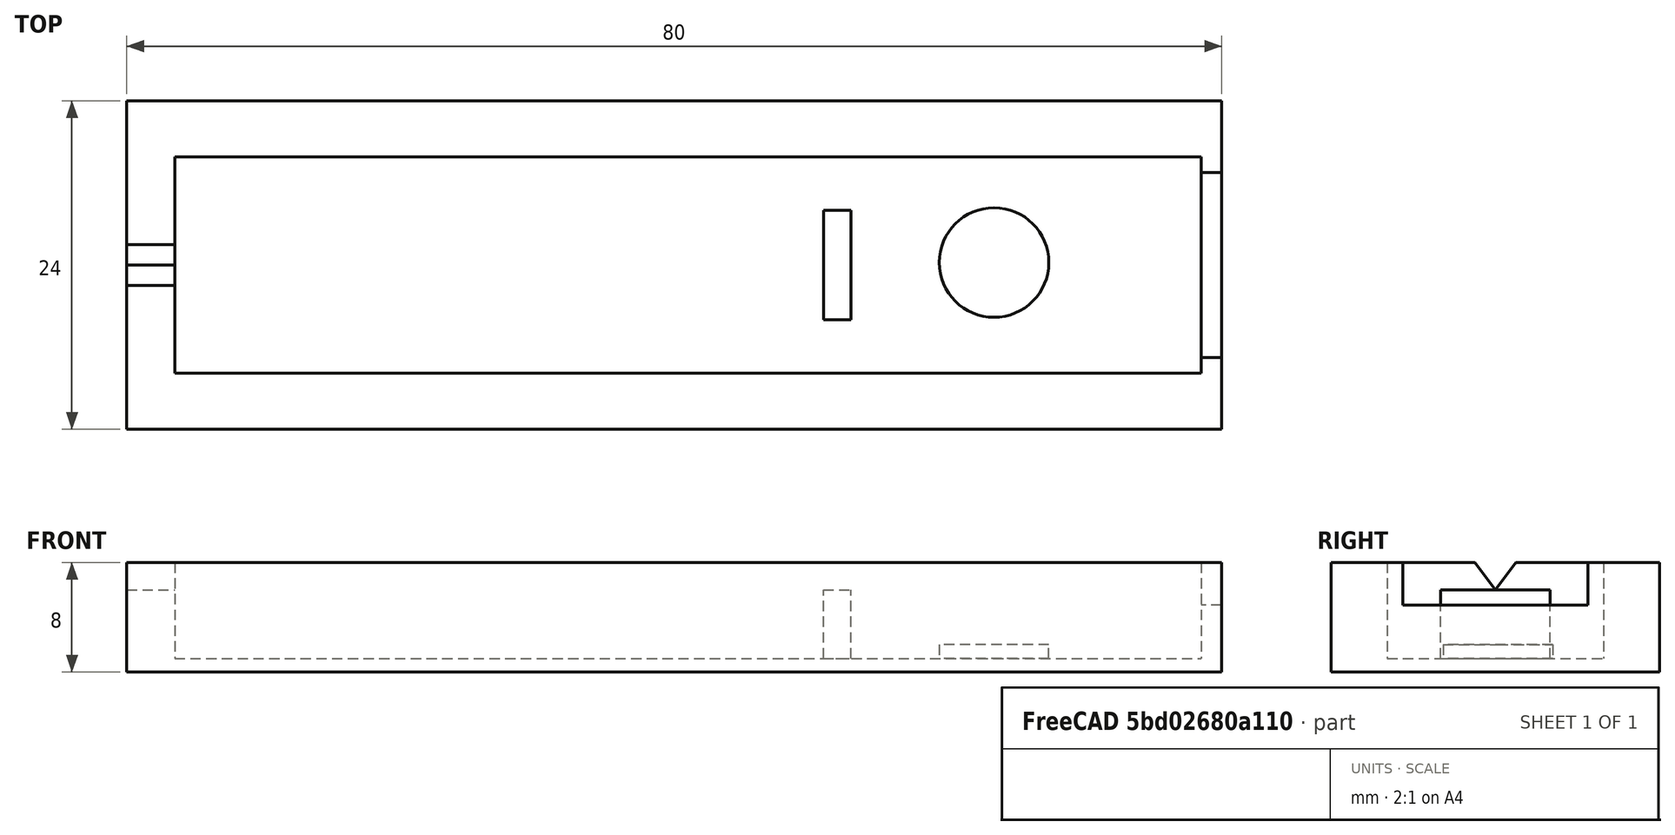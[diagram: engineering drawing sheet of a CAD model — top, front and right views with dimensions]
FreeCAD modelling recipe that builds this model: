
FCSTD DOCUMENT  (FreeCAD 0.19R)
Label: ChargerBuckOnly1
License: All rights reserved
LicenseURL: http://en.wikipedia.org/wiki/All_rights_reserved
objects: Sketcher::SketchObject×7, PartDesign::Pad×3, PartDesign::Pocket×3, PartDesign::Body×1, Mesh::Feature×1
note: 20 computed .brp shape members not serialized (recipe doc carries the construction recipe); baked Part::Feature solids carry a one-line shape summary decoded from their .brp

FEATURE [Sketcher::SketchObject] Sketch
  FullyConstrained = true
  MapMode = 5
  Support = -> [XY_Plane]
  sketch-geometry (4):
    g0: LineSegment StartX=-40 StartY=12 StartZ=0 EndX=40 EndY=12 EndZ=0
    g1: LineSegment StartX=40 StartY=12 StartZ=0 EndX=40 EndY=-12 EndZ=0
    g2: LineSegment StartX=40 StartY=-12 StartZ=0 EndX=-40 EndY=-12 EndZ=0
    g3: LineSegment StartX=-40 StartY=-12 StartZ=0 EndX=-40 EndY=12 EndZ=0
  constraints (11):
    c: Coincident(g0,g1)
    c: Coincident(g1,g2)
    c: Coincident(g2,g3)
    c: Coincident(g3,g0)
    c: Horizontal(g0)
    c: Horizontal(g2)
    c: Vertical(g1)
    c: Vertical(g3)
    c: Symmetric(g0,g2,g-1)
    c: Distance(g1) = 24
    c: Distance(g0,g0) = 80
FEATURE [PartDesign::Pad] Pad
  Direction = (1,1,1)
  Length = 8
  Length2 = 100
  Profile = -> Sketch
  Type = 0
FEATURE [Sketcher::SketchObject] Sketch001
  ExternalGeometry = -> [Pad]
  FullyConstrained = true
  MapMode = 5
  Placement = pos=(0,0,8) rot=(0,0,1;0rad)
  Support = -> [Pad]
  sketch-geometry (4):
    g0: LineSegment StartX=-36.5 StartY=7.9 StartZ=0 EndX=38.5 EndY=7.9 EndZ=0
    g1: LineSegment StartX=38.5 StartY=7.9 StartZ=0 EndX=38.5 EndY=-7.9 EndZ=0
    g2: LineSegment StartX=38.5 StartY=-7.9 StartZ=0 EndX=-36.5 EndY=-7.9 EndZ=0
    g3: LineSegment StartX=-36.5 StartY=-7.9 StartZ=0 EndX=-36.5 EndY=7.9 EndZ=0
  constraints (11):
    c: Coincident(g0,g1)
    c: Coincident(g1,g2)
    c: Coincident(g2,g3)
    c: Coincident(g3,g0)
    c: Horizontal(g0)
    c: Horizontal(g2)
    c: Vertical(g1)
    c: Distance(g0) = 75
    c: Distance(g1) = 15.8
    c: Distance(g1,g-3) = 1.5
    c: Symmetric(g0,g2,g-1)
FEATURE [PartDesign::Pocket] Pocket
  BaseFeature = -> Pad
  Length = 7
  Length2 = 100
  Profile = -> Sketch001
  Type = 0
FEATURE [Sketcher::SketchObject] Sketch002
  ExternalGeometry = -> [Pocket]
  FullyConstrained = true
  MapMode = 5
  Placement = pos=(0,0,1) rot=(0,0,1;0rad)
  Support = -> [Pocket]
  sketch-geometry (4):
    g0: LineSegment StartX=10.9 StartY=4 StartZ=0 EndX=12.9 EndY=4 EndZ=0
    g1: LineSegment StartX=12.9 StartY=4 StartZ=0 EndX=12.9 EndY=-4 EndZ=0
    g2: LineSegment StartX=12.9 StartY=-4 StartZ=0 EndX=10.9 EndY=-4 EndZ=0
    g3: LineSegment StartX=10.9 StartY=-4 StartZ=0 EndX=10.9 EndY=4 EndZ=0
  constraints (11):
    c: Coincident(g0,g1)
    c: Coincident(g1,g2)
    c: Coincident(g2,g3)
    c: Coincident(g3,g0)
    c: Horizontal(g0)
    c: Horizontal(g2)
    c: Vertical(g3)
    c: Distance(g0) = 2
    c: Distance(g1) = 8
    c: Distance(g0,g-3) = 25.6
    c: Symmetric(g1,g0,g-1)
FEATURE [PartDesign::Pad] Pad001
  BaseFeature = -> Pocket
  Direction = (1,1,1)
  Length = 5
  Length2 = 100
  Profile = -> Sketch002
  Type = 0
FEATURE [Sketcher::SketchObject] Sketch003
  ExternalGeometry = -> [Pad001]
  FullyConstrained = true
  MapMode = 5
  Placement = pos=(40,0,0) rot=(0.57735,0.57735,0.57735;2.0944rad)
  Support = -> [Pad001]
  sketch-geometry (4):
    g0: LineSegment StartX=-6.75 StartY=10.8 StartZ=0 EndX=6.75 EndY=10.8 EndZ=0
    g1: LineSegment StartX=6.75 StartY=10.8 StartZ=0 EndX=6.75 EndY=4.9 EndZ=0
    g2: LineSegment StartX=6.75 StartY=4.9 StartZ=0 EndX=-6.75 EndY=4.9 EndZ=0
    g3: LineSegment StartX=-6.75 StartY=4.9 StartZ=0 EndX=-6.75 EndY=10.8 EndZ=0
  constraints (11):
    c: Coincident(g0,g1)
    c: Coincident(g1,g2)
    c: Coincident(g2,g3)
    c: Coincident(g3,g0)
    c: Horizontal(g0)
    c: Vertical(g1)
    c: Vertical(g3)
    c: Distance(g0) = 13.5
    c: Symmetric(g1,g2,g-2)
    c: Distance(g1) = 5.9
    c: Distance(g1,g-3) = 3.1
FEATURE [PartDesign::Pocket] Pocket001
  BaseFeature = -> Pad001
  Length = 5
  Length2 = 100
  Profile = -> Sketch003
  Type = 0
FEATURE [Sketcher::SketchObject] Sketch004
  FullyConstrained = true
  MapMode = 5
  Placement = pos=(0,0,1) rot=(0,0,1;0rad)
  Support = -> [Pocket001]
  sketch-geometry (1):
    g0: Circle CenterX=25 CenterY=0 CenterZ=0 NormalX=0 NormalY=0 NormalZ=1 AngleXU=0 Radius=4
  constraints (3):
    c: PointOnObject(g0,g-1)
    c: Radius(g0) = 4
    c: DistanceX(g0) = 25
FEATURE [Sketcher::SketchObject] Sketch005
  ExternalGeometry = -> [Pocket001]
  FullyConstrained = true
  MapMode = 5
  Placement = pos=(-40,0,0) rot=(0.57735,-0.57735,-0.57735;2.0944rad)
  Support = -> [Pocket001]
  sketch-geometry (3):
    g0: LineSegment StartX=7.5 StartY=16 StartZ=0 EndX=0 EndY=6 EndZ=0
    g1: LineSegment StartX=0 StartY=6 StartZ=0 EndX=-7.5 EndY=16 EndZ=0
    g2: LineSegment StartX=-7.5 StartY=16 StartZ=0 EndX=7.5 EndY=16 EndZ=0
  constraints (8):
    c: PointOnObject(g0,g-2)
    c: Coincident(g0,g1)
    c: Coincident(g1,g2)
    c: Coincident(g2,g0)
    c: Symmetric(g1,g0,g-2)
    c: Distance(g0,g-3) = 2
    c: Distance(g2) = 15
    c: Distance(g0,g-3) = 8
FEATURE [PartDesign::Pocket] Pocket002
  BaseFeature = -> Pocket001
  Length = 5
  Length2 = 100
  Profile = -> Sketch005
  Type = 0
FEATURE [Sketcher::SketchObject] Sketch006
  FullyConstrained = false
  MapMode = 5
  Placement = pos=(0,0,1) rot=(0,0,1;0rad)
  Support = -> [Pocket002]
  sketch-geometry (1):
    g0: Circle CenterX=23.3664 CenterY=0.185267 CenterZ=0 NormalX=0 NormalY=0 NormalZ=1 AngleXU=0 Radius=4.00595
FEATURE [PartDesign::Pad] Pad002
  BaseFeature = -> Pocket002
  Direction = (1,1,1)
  Length = 1
  Length2 = 100
  Profile = -> Sketch006
  Type = 0
FEATURE [PartDesign::Body] Body
  Group = -> [Sketch,Pad,Sketch001,Pocket,Sketch002,Pad001,Sketch003,Pocket001,Sketch004,Sketch005,Pocket002,Sketch006,Pad002]
  Origin = -> Origin
  Tip = -> Pad002
FEATURE [Mesh::Feature] Mesh  label="Pad002 (Meshed)"
